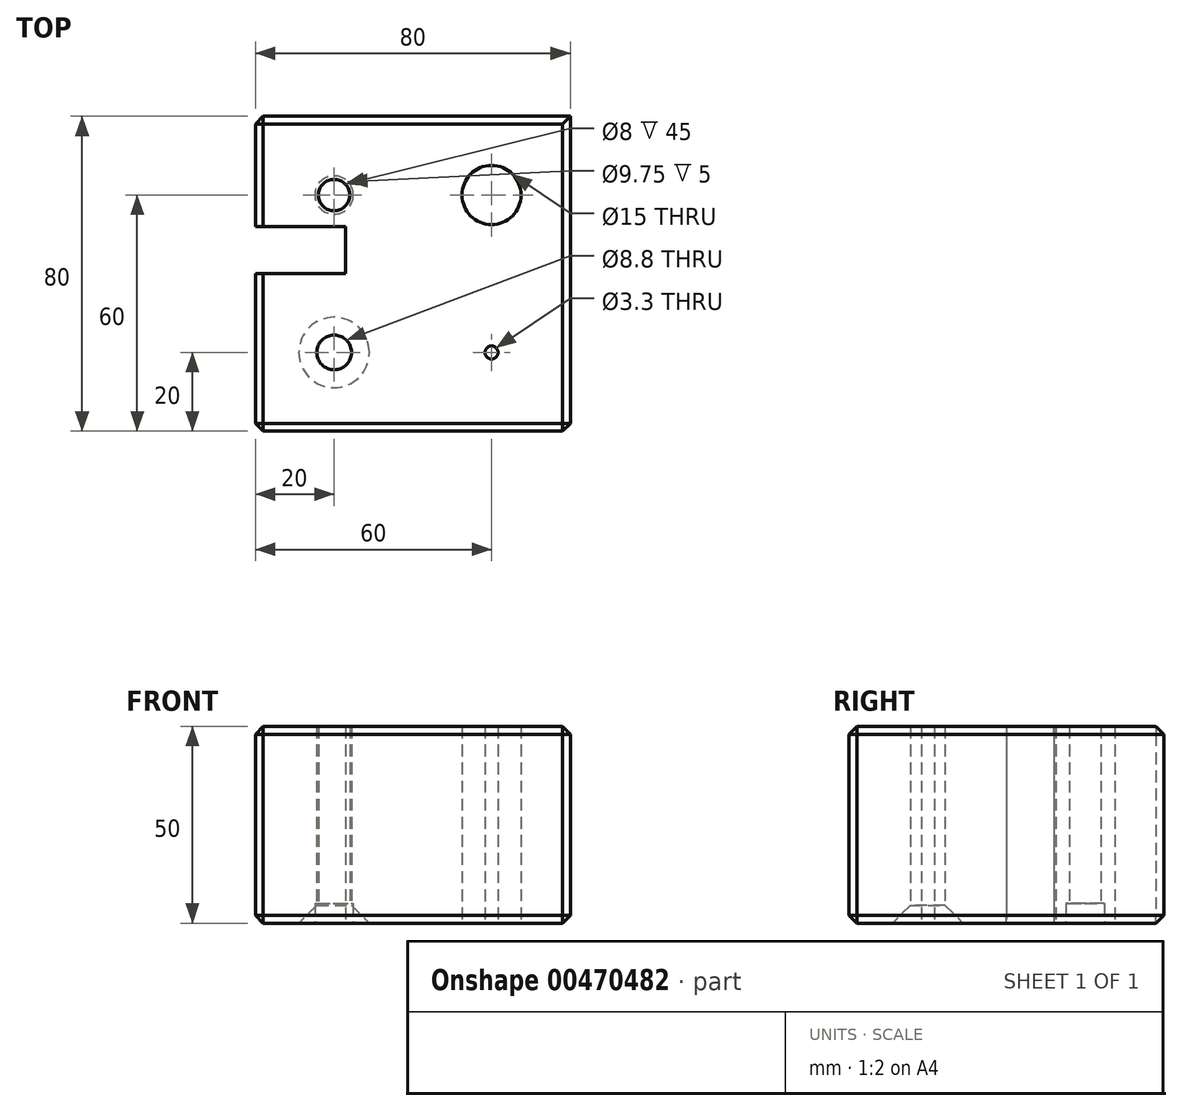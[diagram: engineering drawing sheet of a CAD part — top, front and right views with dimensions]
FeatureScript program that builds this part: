
annotation { "Feature Type Name" : "Feature", "Feature Type Description" : "" }
export const myFeature = defineFeature(function(context is Context, id is Id, definition is map)
    precondition{}
    {
        {
            var Q0;
            Q0=qCreatedBy(makeId("Top.planeOp"),FACE);
            var sketch = newSketch(context, id + "F0", { "sketchPlane" : qUnion([Q0])});
            skLineSegment(sketch, "E0.bottom", {"start": v(40, -40) * mm, "end": v(-40, -40) * mm});
            skLineSegment(sketch, "E0.top", {"start": v(40, 40) * mm, "end": v(-40, 40) * mm});
            skLineSegment(sketch, "E0.left", {"start": v(40, -40) * mm, "end": v(40, 40) * mm});
            skLineSegment(sketch, "E0.right", {"start": v(-40, -40) * mm, "end": v(-40, 40) * mm});
            skPoint(sketch, "E0.middle", {"position": v(0, 0) * mm});
            skPoint(sketch, "E1", {"position": v(-20, 20) * mm});
            skPoint(sketch, "E2", {"position": v(20, 20) * mm});
            skPoint(sketch, "E3", {"position": v(-20, -20) * mm});
            skPoint(sketch, "E4", {"position": v(20, -20) * mm});
            skPoint(sketch, "E5.start.orphan", {"position": v(0, -40) * mm});
            skPoint(sketch, "E6.trimOffspring.end.orphan", {"position": v(40, 0) * mm});
            skPoint(sketch, "E7.start.orphan", {"position": v(-40, 0) * mm});
            skLineSegment(sketch, "E8.bottom", {"start": v(-40, 0) * mm, "end": v(-17.1, 0) * mm});
            skLineSegment(sketch, "E8.top", {"start": v(-40, 12) * mm, "end": v(-17.1, 12) * mm});
            skLineSegment(sketch, "E8.right", {"start": v(-17.1, 0) * mm, "end": v(-17.1, 12) * mm});
            skSolve(sketch);
        }
        {
            var Q0;
            Q0=makeQuery(id+"F0.imprint","IMPRINT",FACE,{"disambiguationData":[TD([[makeQuery(id+"F0.imprint","IMPRINT",EDGE,{"derivedFrom":sQuery(id+"F0.wireOp",EDGE,"E0.bottom")}),-1.0]])]});
            extrude(context, id + "F1", {"entities" : qUnion([Q0]), "depth" : 50 * mm});
        }
        {
            var Q0;
            Q0=sQuery(id+"F0.wireOp",VERTEX,"E1");
            var Q1;
            Q1=makeQuery(id+"F1.opExtrude","SWEPT_BODY",BODY,{"disambiguationData":[OSD([sQuery(id+"F0.wireOp",EDGE,"E0.bottom"),sQuery(id+"F0.wireOp",EDGE,"E0.top"),sQuery(id+"F0.wireOp",EDGE,"E0.left"),sQuery(id+"F0.wireOp",EDGE,"E0.right")])]});
            hole(context, id + "F2", {"style" : HoleStyle.C_BORE, "endStyle" : HoleEndStyle.THROUGH, "oppositeDirection" : true, "holeDiameter" : 8 * mm, "cBoreDiameter" : 9.75 * mm, "cBoreDepth" : 5 * mm, "tappedDepth" : 10 * mm, "tapClearance" : 3, "startFromSketch" : true, "locations" : qUnion([Q0]), "scope" : qUnion([Q1])});
        }
        {
            var Q0;
            Q0=sQuery(id+"F0.wireOp",VERTEX,"E2");
            var Q1;
            Q1=makeQuery(id+"F1.opExtrude","SWEPT_BODY",BODY,{"disambiguationData":[OSD([sQuery(id+"F0.wireOp",EDGE,"E0.bottom"),sQuery(id+"F0.wireOp",EDGE,"E0.top"),sQuery(id+"F0.wireOp",EDGE,"E0.left"),sQuery(id+"F0.wireOp",EDGE,"E0.right")])]});
            hole(context, id + "F3", {"style" : HoleStyle.SIMPLE, "endStyle" : HoleEndStyle.THROUGH, "oppositeDirection" : true, "holeDiameter" : 15 * mm, "tappedDepth" : 10 * mm, "tapClearance" : 3, "startFromSketch" : true, "locations" : qUnion([Q0]), "scope" : qUnion([Q1])});
        }
        {
            var Q0;
            Q0=sQuery(id+"F0.wireOp",VERTEX,"E3");
            var Q1;
            Q1=makeQuery(id+"F1.opExtrude","SWEPT_BODY",BODY,{"disambiguationData":[OSD([sQuery(id+"F0.wireOp",EDGE,"E0.bottom"),sQuery(id+"F0.wireOp",EDGE,"E0.top"),sQuery(id+"F0.wireOp",EDGE,"E0.left"),sQuery(id+"F0.wireOp",EDGE,"E0.right")])]});
            hole(context, id + "F4", {"style" : HoleStyle.C_SINK, "endStyle" : HoleEndStyle.THROUGH, "oppositeDirection" : true, "standardTappedOrClearance" : lookupTablePath({ "standard" : "ISO", "fit" : "Normal", "size" : "M8", "type" : "Clearance" }), "standardBlindInLast" : lookupTablePath({ "fit" : "Standard", "standard" : "ISO", "size" : "M8", "type" : "Clearance" }), "holeDiameter" : 8.8 * mm, "cSinkDiameter" : 17.92 * mm, "cSinkAngle" : 90 * degree, "tappedDepth" : 10 * mm, "tapClearance" : 3, "startFromSketch" : true, "locations" : qUnion([Q0]), "scope" : qUnion([Q1])});
        }
        {
            var Q0;
            Q0=sQuery(id+"F0.wireOp",VERTEX,"E4");
            var Q1;
            Q1=makeQuery(id+"F1.opExtrude","SWEPT_BODY",BODY,{"disambiguationData":[OSD([sQuery(id+"F0.wireOp",EDGE,"E0.bottom"),sQuery(id+"F0.wireOp",EDGE,"E0.top"),sQuery(id+"F0.wireOp",EDGE,"E0.left"),sQuery(id+"F0.wireOp",EDGE,"E0.right")])]});
            hole(context, id + "F5", {"style" : HoleStyle.SIMPLE, "endStyle" : HoleEndStyle.THROUGH, "oppositeDirection" : true, "standardTappedOrClearance" : lookupTablePath({ "standard" : "ISO", "engagement" : "75%", "pitch" : "0.7 mm", "size" : "M4", "type" : "Tapped" }), "standardBlindInLast" : lookupTablePath({ "standard" : "ISO", "engagement" : "75%", "pitch" : "0.7 mm", "size" : "M4", "type" : "Tapped" }), "holeDiameter" : 3.3 * mm, "showTappedDepth" : true, "isTappedThrough" : true, "tappedDepth" : 10 * mm, "tapClearance" : 3, "startFromSketch" : true, "locations" : qUnion([Q0]), "scope" : qUnion([Q1]), "majorDiameter" : 4 * mm});
        }
        {
            var Q0;
            Q0=makeQuery(id+"F1.opExtrude","SWEPT_EDGE",EDGE,{"disambiguationData":[OSD([sQuery(id+"F0.wireOp",EDGE,"E0.top"),sQuery(id+"F0.wireOp",EDGE,"E0.right")])]});
            var Q1;
            Q1=makeQuery(id+"F1.opExtrude","CAP_EDGE",EDGE,{"disambiguationData":[OSD([sQuery(id+"F0.wireOp",EDGE,"E0.right")])],"isStart":false});
            var Q2;
            Q2=makeQuery(id+"F1.opExtrude","SWEPT_EDGE",EDGE,{"disambiguationData":[OSD([sQuery(id+"F0.wireOp",EDGE,"E0.bottom"),sQuery(id+"F0.wireOp",EDGE,"E0.right")])]});
            var Q3;
            Q3=makeQuery(id+"F1.opExtrude","CAP_EDGE",EDGE,{"disambiguationData":[OSD([sQuery(id+"F0.wireOp",EDGE,"E0.right")])],"isStart":true});
            var Q4;
            Q4=makeQuery(id+"F1.opExtrude","CAP_EDGE",EDGE,{"disambiguationData":[OSD([sQuery(id+"F0.wireOp",EDGE,"E0.top")])],"isStart":true});
            var Q5;
            Q5=makeQuery(id+"F1.opExtrude","CAP_EDGE",EDGE,{"disambiguationData":[OSD([sQuery(id+"F0.wireOp",EDGE,"E0.bottom")])],"isStart":true});
            var Q6;
            Q6=makeQuery(id+"F1.opExtrude","CAP_EDGE",EDGE,{"disambiguationData":[OSD([sQuery(id+"F0.wireOp",EDGE,"E0.left")])],"isStart":true});
            var Q7;
            Q7=makeQuery(id+"F1.opExtrude","CAP_EDGE",EDGE,{"disambiguationData":[OSD([sQuery(id+"F0.wireOp",EDGE,"E0.left")])],"isStart":false});
            var Q8;
            Q8=makeQuery(id+"F1.opExtrude","CAP_EDGE",EDGE,{"disambiguationData":[OSD([sQuery(id+"F0.wireOp",EDGE,"E0.top")])],"isStart":false});
            var Q9;
            Q9=makeQuery(id+"F1.opExtrude","CAP_EDGE",EDGE,{"disambiguationData":[OSD([sQuery(id+"F0.wireOp",EDGE,"E0.bottom")])],"isStart":false});
            var Q10;
            Q10=makeQuery(id+"F1.opExtrude","SWEPT_EDGE",EDGE,{"disambiguationData":[OSD([sQuery(id+"F0.wireOp",EDGE,"E0.bottom"),sQuery(id+"F0.wireOp",EDGE,"E0.left")])]});
            chamfer(context, id + "F6", {"entities" : qUnion([Q0, Q1, Q2, Q3, Q4, Q5, Q6, Q7, Q8, Q9, Q10]), "chamferType" : ChamferType.OFFSET_ANGLE, "width" : 2 * mm, "oppositeDirection" : false, "angle" : 45 * degree, "tangentPropagation" : true});
        }
    });
